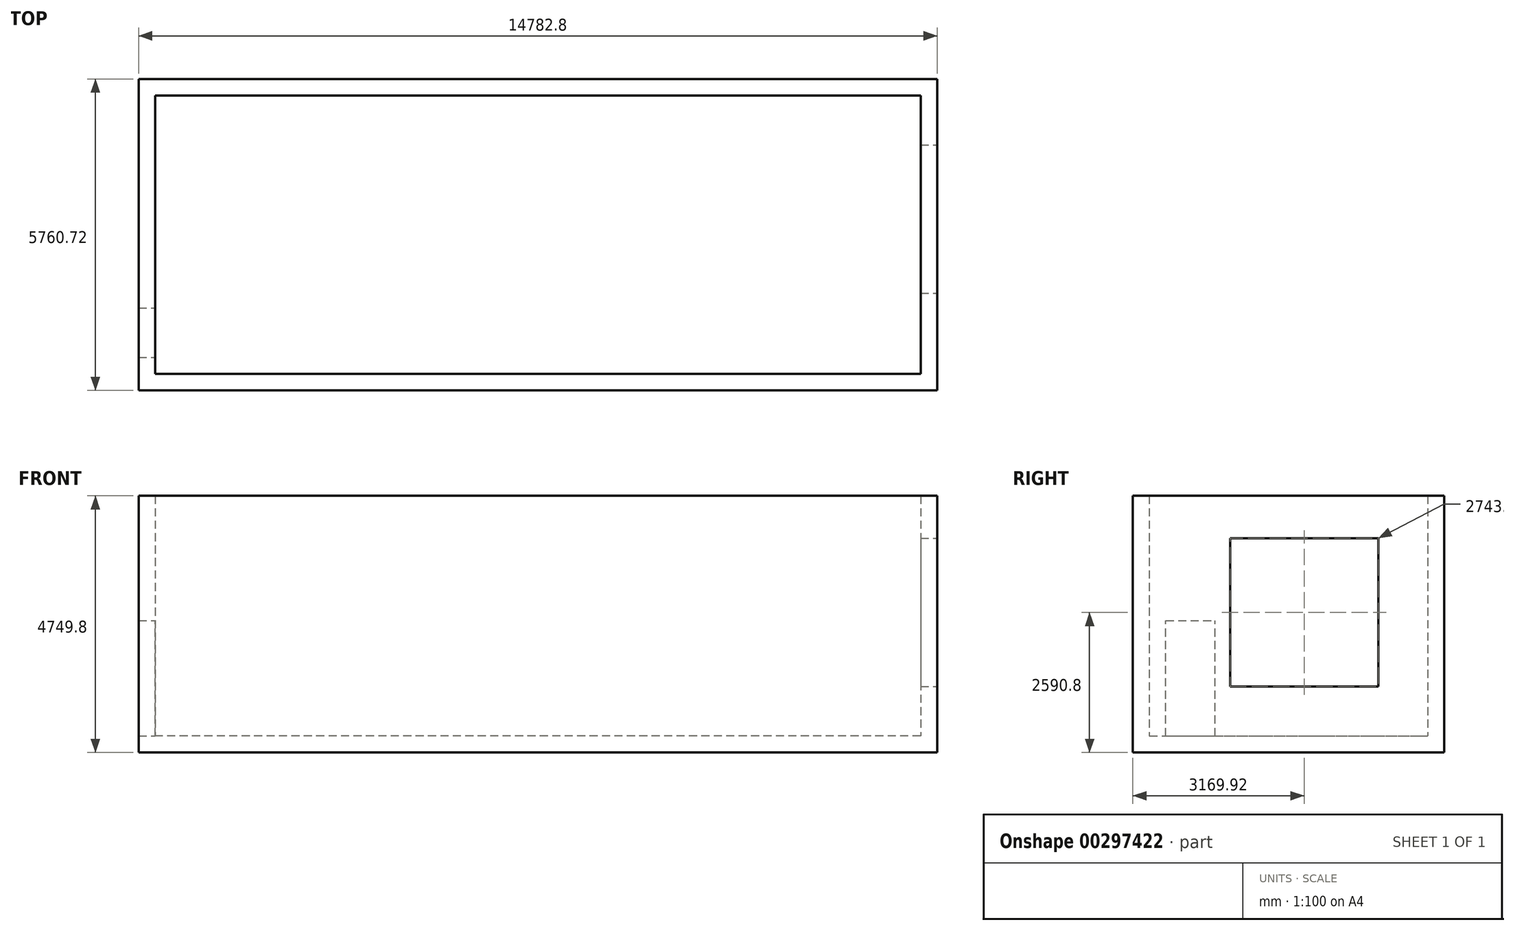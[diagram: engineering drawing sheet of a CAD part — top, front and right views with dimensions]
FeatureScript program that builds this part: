
annotation { "Feature Type Name" : "Feature", "Feature Type Description" : "" }
export const myFeature = defineFeature(function(context is Context, id is Id, definition is map)
    precondition{}
    {
        {
            var Q0;
            Q0=qCreatedBy(makeId("Top.planeOp"),FACE);
            var sketch = newSketch(context, id + "F0", { "sketchPlane" : qUnion([Q0])});
            skLineSegment(sketch, "E0.bottom", {"start": v(7086.6, -2575.56) * mm, "end": v(-7086.6, -2575.56) * mm});
            skLineSegment(sketch, "E0.top", {"start": v(7086.6, 2575.56) * mm, "end": v(-7086.6, 2575.56) * mm});
            skLineSegment(sketch, "E0.left", {"start": v(7086.6, -2575.56) * mm, "end": v(7086.6, 2575.56) * mm});
            skLineSegment(sketch, "E0.right", {"start": v(-7086.6, -2575.56) * mm, "end": v(-7086.6, 2575.56) * mm});
            skPoint(sketch, "E0.middle", {"position": v(0, 0) * mm});
            skLineSegment(sketch, "E1.0", {"start": v(-7391.4, -2880.36) * mm, "end": v(-7391.4, 2880.36) * mm});
            skLineSegment(sketch, "E1.1", {"start": v(7391.4, -2880.36) * mm, "end": v(-7391.4, -2880.36) * mm});
            skLineSegment(sketch, "E1.2", {"start": v(7391.4, -2880.36) * mm, "end": v(7391.4, 2880.36) * mm});
            skLineSegment(sketch, "E1.3", {"start": v(7391.4, 2880.36) * mm, "end": v(-7391.4, 2880.36) * mm});
            skSolve(sketch);
        }
        {
            var Q0;
            Q0=makeQuery(id+"F0.imprint","IMPRINT",FACE,{"disambiguationData":[TD([[makeQuery(id+"F0.imprint","IMPRINT",EDGE,{"derivedFrom":sQuery(id+"F0.wireOp",EDGE,"E0.bottom")}),1.0]])]});
            extrude(context, id + "F1", {"entities" : qUnion([Q0]), "depth" : 4445 * mm, "offsetDistance" : 25.4 * mm});
        }
        {
            var Q0;
            Q0=makeQuery(id+"F1.opExtrude","SWEPT_FACE",FACE,{"disambiguationData":[OSD([sQuery(id+"F0.wireOp",EDGE,"E1.0")])]});
            var sketch = newSketch(context, id + "F2", { "sketchPlane" : qUnion([Q0])});
            skLineSegment(sketch, "E2.bottom", {"start": v(-2880.36, 0) * mm, "end": v(2880.36, 0) * mm});
            skLineSegment(sketch, "E2.top", {"start": v(-2880.36, -304.8) * mm, "end": v(2880.36, -304.8) * mm});
            skLineSegment(sketch, "E2.left", {"start": v(-2880.36, 0) * mm, "end": v(-2880.36, -304.8) * mm});
            skLineSegment(sketch, "E2.right", {"start": v(2880.36, 0) * mm, "end": v(2880.36, -304.8) * mm});
            skSolve(sketch);
        }
        {
            var Q0;
            Q0=makeQuery(id+"F2.imprint","IMPRINT",FACE,{"disambiguationData":[TD([[makeQuery(id+"F2.imprint","IMPRINT",EDGE,{"derivedFrom":sQuery(id+"F2.wireOp",EDGE,"E2.bottom")}),1.0]])]});
            var Q1;
            Q1=makeQuery(id+"F1.opExtrude","SWEPT_FACE",FACE,{"disambiguationData":[OSD([sQuery(id+"F0.wireOp",EDGE,"E1.2")])]});
            extrude(context, id + "F3", {"entities" : qUnion([Q0]), "operationType" : NewBodyOperationType.ADD, "endBound" : BoundingType.UP_TO_SURFACE, "oppositeDirection" : true, "endBoundEntityFace" : qUnion([Q1]), "depth" : 25.4 * mm});
        }
        {
            var Q0;
            {var subQ0=sQuery(id+"F0.wireOp",EDGE,"E1.2");Q0=makeQuery(id+"F3.boolean.opBoolean","MERGE",FACE,{"derivedFrom":[makeQuery(id+"F1.opExtrude","SWEPT_FACE",FACE,{"disambiguationData":[OSD([subQ0])]}),makeQuery(id+"F3.opExtrude","CAP_FACE",FACE,{"disambiguationData":[OSD([subQ0])],"isStart":false})]});}
            var sketch = newSketch(context, id + "F4", { "sketchPlane" : qUnion([Q0])});
            skLineSegment(sketch, "E3.bottom", {"start": v(-1082.04, 3657.6) * mm, "end": v(1661.16, 3657.6) * mm});
            skLineSegment(sketch, "E3.top", {"start": v(-1082.04, 914.4) * mm, "end": v(1661.16, 914.4) * mm});
            skLineSegment(sketch, "E3.left", {"start": v(-1082.04, 3657.6) * mm, "end": v(-1082.04, 914.4) * mm});
            skLineSegment(sketch, "E3.right", {"start": v(1661.16, 3657.6) * mm, "end": v(1661.16, 914.4) * mm});
            skSolve(sketch);
        }
        {
            var Q0;
            Q0=qSketchRegion(id+"F4",true);
            extrude(context, id + "F5", {"entities" : qUnion([Q0]), "operationType" : NewBodyOperationType.REMOVE, "endBound" : BoundingType.UP_TO_NEXT, "oppositeDirection" : true, "depth" : 25.4 * mm});
        }
        {
            var Q0;
            Q0=makeQuery(id+"F1.opExtrude","SWEPT_FACE",FACE,{"disambiguationData":[OSD([sQuery(id+"F0.wireOp",EDGE,"E0.right")])]});
            var sketch = newSketch(context, id + "F6", { "sketchPlane" : qUnion([Q0])});
            skLineSegment(sketch, "E4.bottom", {"start": v(-2270.76, 0) * mm, "end": v(-1356.36, 0) * mm});
            skLineSegment(sketch, "E4.top", {"start": v(-2270.76, 2133.6) * mm, "end": v(-1356.36, 2133.6) * mm});
            skLineSegment(sketch, "E4.left", {"start": v(-2270.76, 0) * mm, "end": v(-2270.76, 2133.6) * mm});
            skLineSegment(sketch, "E4.right", {"start": v(-1356.36, 0) * mm, "end": v(-1356.36, 2133.6) * mm});
            skSolve(sketch);
        }
        {
            var Q0;
            Q0=qSketchRegion(id+"F6",true);
            extrude(context, id + "F7", {"entities" : qUnion([Q0]), "operationType" : NewBodyOperationType.REMOVE, "endBound" : BoundingType.UP_TO_NEXT, "oppositeDirection" : true, "depth" : 25.4 * mm});
        }
    });
